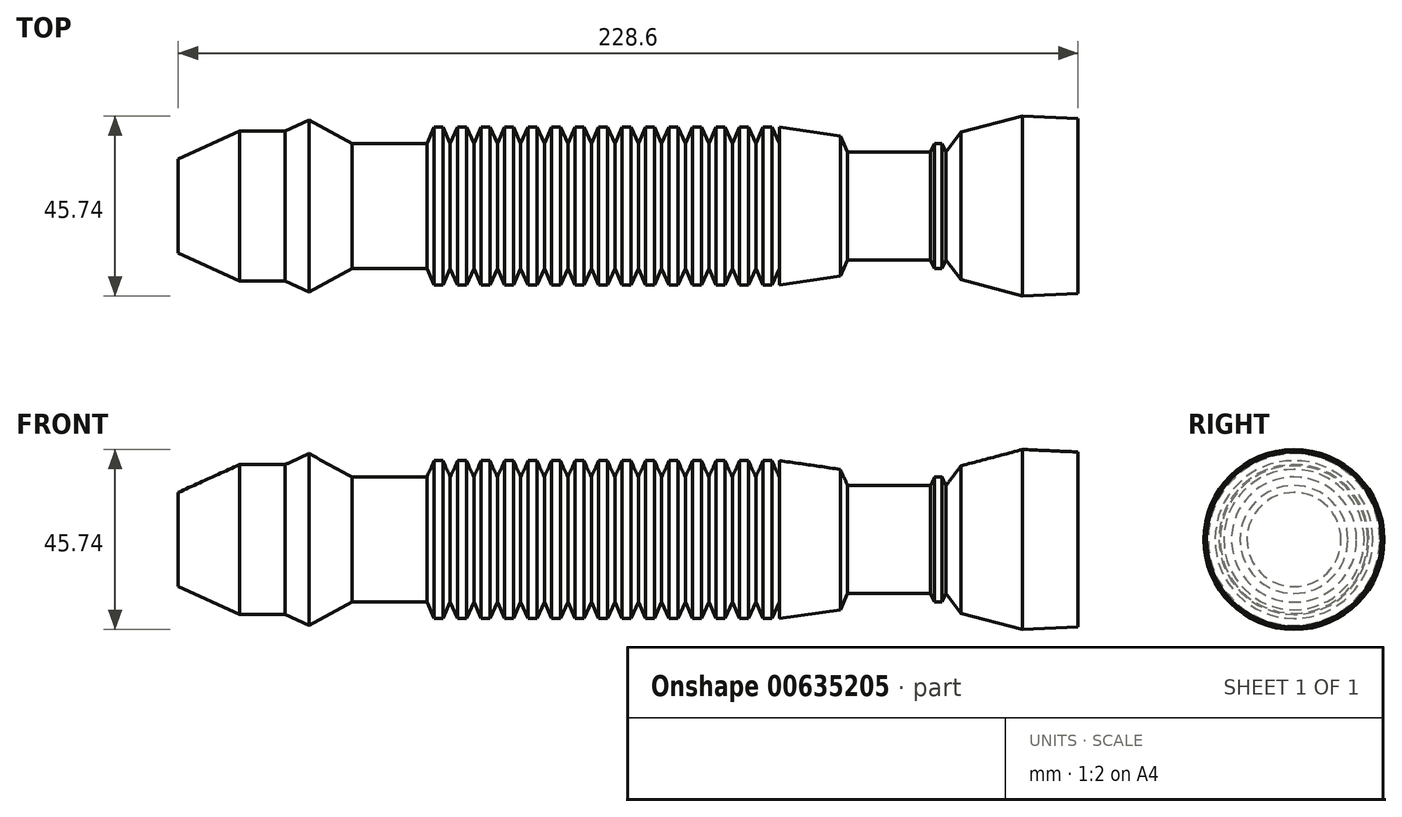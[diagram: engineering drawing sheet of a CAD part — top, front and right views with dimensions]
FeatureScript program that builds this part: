
annotation { "Feature Type Name" : "Feature", "Feature Type Description" : "" }
export const myFeature = defineFeature(function(context is Context, id is Id, definition is map)
    precondition{}
    {
        {
            var Q0;
            Q0=qCreatedBy(makeId("Top.planeOp"),FACE);
            var sketch = newSketch(context, id + "F0", { "sketchPlane" : qUnion([Q0])});
            skLineSegment(sketch, "E0", {"start": v(0, 0) * mm, "end": v(228.6, 0) * mm});
            skLineSegment(sketch, "E1", {"start": v(228.6, 0) * mm, "end": v(228.6, 22.23) * mm});
            skLineSegment(sketch, "E2.MirrorCS", {"start": v(228.6, 0) * mm, "end": v(228.6, -22.23) * mm});
            skLineSegment(sketch, "E3", {"start": v(228.6, 22.23) * mm, "end": v(214.54, 22.87) * mm});
            skLineSegment(sketch, "E4", {"start": v(195.05, 13.7) * mm, "end": v(194.06, 15.9) * mm});
            skLineSegment(sketch, "E5", {"start": v(194.06, 15.9) * mm, "end": v(192.18, 15.9) * mm});
            skLineSegment(sketch, "E6", {"start": v(192.18, 15.9) * mm, "end": v(191.1, 13.7) * mm});
            skLineSegment(sketch, "E7", {"start": v(191.1, 13.7) * mm, "end": v(170.09, 13.7) * mm});
            skLineSegment(sketch, "E8", {"start": v(170.09, 13.7) * mm, "end": v(168.21, 17.83) * mm});
            skLineSegment(sketch, "E9", {"start": v(168.21, 17.83) * mm, "end": v(152.7, 20.05) * mm});
            skLineSegment(sketch, "E10", {"start": v(152.7, 20.05) * mm, "end": v(152.7, 15.9) * mm});
            skLineSegment(sketch, "E11", {"start": v(152.7, 15.9) * mm, "end": v(150.81, 20.05) * mm});
            skLineSegment(sketch, "E12", {"start": v(150.81, 20.05) * mm, "end": v(148.62, 20.05) * mm});
            skLineSegment(sketch, "E13", {"start": v(149.72, 20.05) * mm, "end": v(149.72, 16.16) * mm});
            skPoint(sketch, "E13.endSnap0", {"position": v(149.72, 20.05) * mm});
            skLineSegment(sketch, "E14.MirrorCS", {"start": v(146.73, 15.9) * mm, "end": v(148.62, 20.05) * mm});
            skLineSegment(sketch, "E15", {"start": v(146.73, 15.9) * mm, "end": v(152.7, 15.9) * mm});
            skLineSegment(sketch, "E16.1.0.0", {"start": v(146.73, 15.9) * mm, "end": v(144.84, 20.05) * mm});
            skLineSegment(sketch, "E16.1.0.1", {"start": v(140.76, 15.9) * mm, "end": v(142.65, 20.05) * mm});
            skLineSegment(sketch, "E16.1.0.2", {"start": v(144.84, 20.05) * mm, "end": v(142.65, 20.05) * mm});
            skLineSegment(sketch, "E16.2.0.0", {"start": v(140.76, 15.9) * mm, "end": v(138.87, 20.05) * mm});
            skLineSegment(sketch, "E16.2.0.1", {"start": v(134.8, 15.9) * mm, "end": v(136.68, 20.05) * mm});
            skLineSegment(sketch, "E16.2.0.2", {"start": v(138.87, 20.05) * mm, "end": v(136.68, 20.05) * mm});
            skLineSegment(sketch, "E16.3.0.0", {"start": v(134.8, 15.9) * mm, "end": v(132.9, 20.05) * mm});
            skLineSegment(sketch, "E16.3.0.1", {"start": v(128.82, 15.9) * mm, "end": v(130.71, 20.05) * mm});
            skLineSegment(sketch, "E16.3.0.2", {"start": v(132.9, 20.05) * mm, "end": v(130.71, 20.05) * mm});
            skLineSegment(sketch, "E16.4.0.0", {"start": v(128.82, 15.9) * mm, "end": v(126.94, 20.05) * mm});
            skLineSegment(sketch, "E16.4.0.1", {"start": v(122.85, 15.9) * mm, "end": v(124.74, 20.05) * mm});
            skLineSegment(sketch, "E16.4.0.2", {"start": v(126.94, 20.05) * mm, "end": v(124.74, 20.05) * mm});
            skLineSegment(sketch, "E16.5.0.0", {"start": v(122.85, 15.9) * mm, "end": v(120.97, 20.05) * mm});
            skLineSegment(sketch, "E16.5.0.1", {"start": v(116.89, 15.9) * mm, "end": v(118.77, 20.05) * mm});
            skLineSegment(sketch, "E16.5.0.2", {"start": v(120.97, 20.05) * mm, "end": v(118.77, 20.05) * mm});
            skLineSegment(sketch, "E16.6.0.0", {"start": v(116.89, 15.9) * mm, "end": v(115, 20.05) * mm});
            skLineSegment(sketch, "E16.6.0.1", {"start": v(110.92, 15.9) * mm, "end": v(112.8, 20.05) * mm});
            skLineSegment(sketch, "E16.6.0.2", {"start": v(115, 20.05) * mm, "end": v(112.8, 20.05) * mm});
            skLineSegment(sketch, "E16.7.0.0", {"start": v(110.92, 15.9) * mm, "end": v(109.03, 20.05) * mm});
            skLineSegment(sketch, "E16.7.0.1", {"start": v(104.95, 15.9) * mm, "end": v(106.83, 20.05) * mm});
            skLineSegment(sketch, "E16.7.0.2", {"start": v(109.03, 20.05) * mm, "end": v(106.83, 20.05) * mm});
            skLineSegment(sketch, "E16.8.0.0", {"start": v(104.95, 15.9) * mm, "end": v(103.06, 20.05) * mm});
            skLineSegment(sketch, "E16.8.0.1", {"start": v(98.98, 15.9) * mm, "end": v(100.87, 20.05) * mm});
            skLineSegment(sketch, "E16.8.0.2", {"start": v(103.06, 20.05) * mm, "end": v(100.87, 20.05) * mm});
            skLineSegment(sketch, "E16.9.0.0", {"start": v(98.98, 15.9) * mm, "end": v(97.09, 20.05) * mm});
            skLineSegment(sketch, "E16.9.0.1", {"start": v(93, 15.9) * mm, "end": v(94.9, 20.05) * mm});
            skLineSegment(sketch, "E16.9.0.2", {"start": v(97.09, 20.05) * mm, "end": v(94.9, 20.05) * mm});
            skLineSegment(sketch, "E16.10.0.0", {"start": v(93, 15.9) * mm, "end": v(91.12, 20.05) * mm});
            skLineSegment(sketch, "E16.10.0.1", {"start": v(87.04, 15.9) * mm, "end": v(88.93, 20.05) * mm});
            skLineSegment(sketch, "E16.10.0.2", {"start": v(91.12, 20.05) * mm, "end": v(88.93, 20.05) * mm});
            skLineSegment(sketch, "E16.11.0.0", {"start": v(87.04, 15.9) * mm, "end": v(85.15, 20.05) * mm});
            skLineSegment(sketch, "E16.11.0.1", {"start": v(81.07, 15.9) * mm, "end": v(82.96, 20.05) * mm});
            skLineSegment(sketch, "E16.11.0.2", {"start": v(85.15, 20.05) * mm, "end": v(82.96, 20.05) * mm});
            skLineSegment(sketch, "E16.12.0.0", {"start": v(81.07, 15.9) * mm, "end": v(79.18, 20.05) * mm});
            skLineSegment(sketch, "E16.12.0.1", {"start": v(75.1, 15.9) * mm, "end": v(76.99, 20.05) * mm});
            skLineSegment(sketch, "E16.12.0.2", {"start": v(79.18, 20.05) * mm, "end": v(76.99, 20.05) * mm});
            skLineSegment(sketch, "E16.13.0.0", {"start": v(75.1, 15.9) * mm, "end": v(73.21, 20.05) * mm});
            skLineSegment(sketch, "E16.13.0.1", {"start": v(69.13, 15.9) * mm, "end": v(71.02, 20.05) * mm});
            skLineSegment(sketch, "E16.13.0.2", {"start": v(73.21, 20.05) * mm, "end": v(71.02, 20.05) * mm});
            skLineSegment(sketch, "E16.14.0.0", {"start": v(69.13, 15.9) * mm, "end": v(67.24, 20.05) * mm});
            skLineSegment(sketch, "E16.14.0.1", {"start": v(63.16, 15.9) * mm, "end": v(65.05, 20.05) * mm});
            skLineSegment(sketch, "E16.14.0.2", {"start": v(67.24, 20.05) * mm, "end": v(65.05, 20.05) * mm});
            skLineSegment(sketch, "E16.direction1", {"start": v(152.7, 15.9) * mm, "end": v(146.73, 15.9) * mm, "construction": true});
            skLineSegment(sketch, "E17", {"start": v(63.16, 15.9) * mm, "end": v(44.12, 15.9) * mm});
            skLineSegment(sketch, "E18", {"start": v(44.12, 15.9) * mm, "end": v(33.25, 21.82) * mm});
            skLineSegment(sketch, "E19", {"start": v(33.25, 21.82) * mm, "end": v(27.1, 19.02) * mm});
            skLineSegment(sketch, "E20", {"start": v(27.1, 19.02) * mm, "end": v(15.54, 19.02) * mm});
            skLineSegment(sketch, "E21", {"start": v(15.54, 19.02) * mm, "end": v(8.67, 15.9) * mm});
            skLineSegment(sketch, "E22", {"start": v(8.67, 15.9) * mm, "end": v(0, 11.95) * mm});
            skLineSegment(sketch, "E23", {"start": v(0, 11.95) * mm, "end": v(0, 0) * mm});
            skLineSegment(sketch, "E24", {"start": v(195.05, 13.7) * mm, "end": v(198.9, 18.73) * mm});
            skLineSegment(sketch, "E25", {"start": v(198.9, 18.73) * mm, "end": v(214.54, 22.87) * mm});
            skLineSegment(sketch, "E26", {"start": v(170.09, 13.7) * mm, "end": v(199.2, 46.7) * mm});
            skLineSegment(sketch, "E27", {"start": v(199.2, 46.7) * mm, "end": v(303.8, 26.09) * mm});
            skLineSegment(sketch, "E28", {"start": v(303.8, 26.09) * mm, "end": v(203.6, 31.55) * mm});
            skLineSegment(sketch, "E29", {"start": v(203.6, 31.55) * mm, "end": v(195.05, 13.7) * mm});
            skSolve(sketch);
        }
        {
            var Q0;
            {var subQ3=sQuery(id+"F0.wireOp",EDGE,"E11");Q0=makeQuery(id+"F0.imprint","IMPRINT",FACE,{"disambiguationData":[TD([[makeQuery(id+"F0.imprint","IMPRINT",EDGE,{"derivedFrom":subQ3}),1.0]])]});}
            var Q1;
            Q1=makeQuery(id+"F0.imprint","IMPRINT",FACE,{"disambiguationData":[TD([[makeQuery(id+"F0.imprint","IMPRINT",EDGE,{"derivedFrom":sQuery(id+"F0.wireOp",EDGE,"E0")}),1.0]])]});
            var Q2;
            Q2=sQuery(id+"F0.wireOp",EDGE,"E0");
            revolve(context, id + "F1", {"entities" : qUnion([Q0, Q1]), "axis" : qUnion([Q2]), "revolveType" : RevolveType.FULL});
        }
    });
